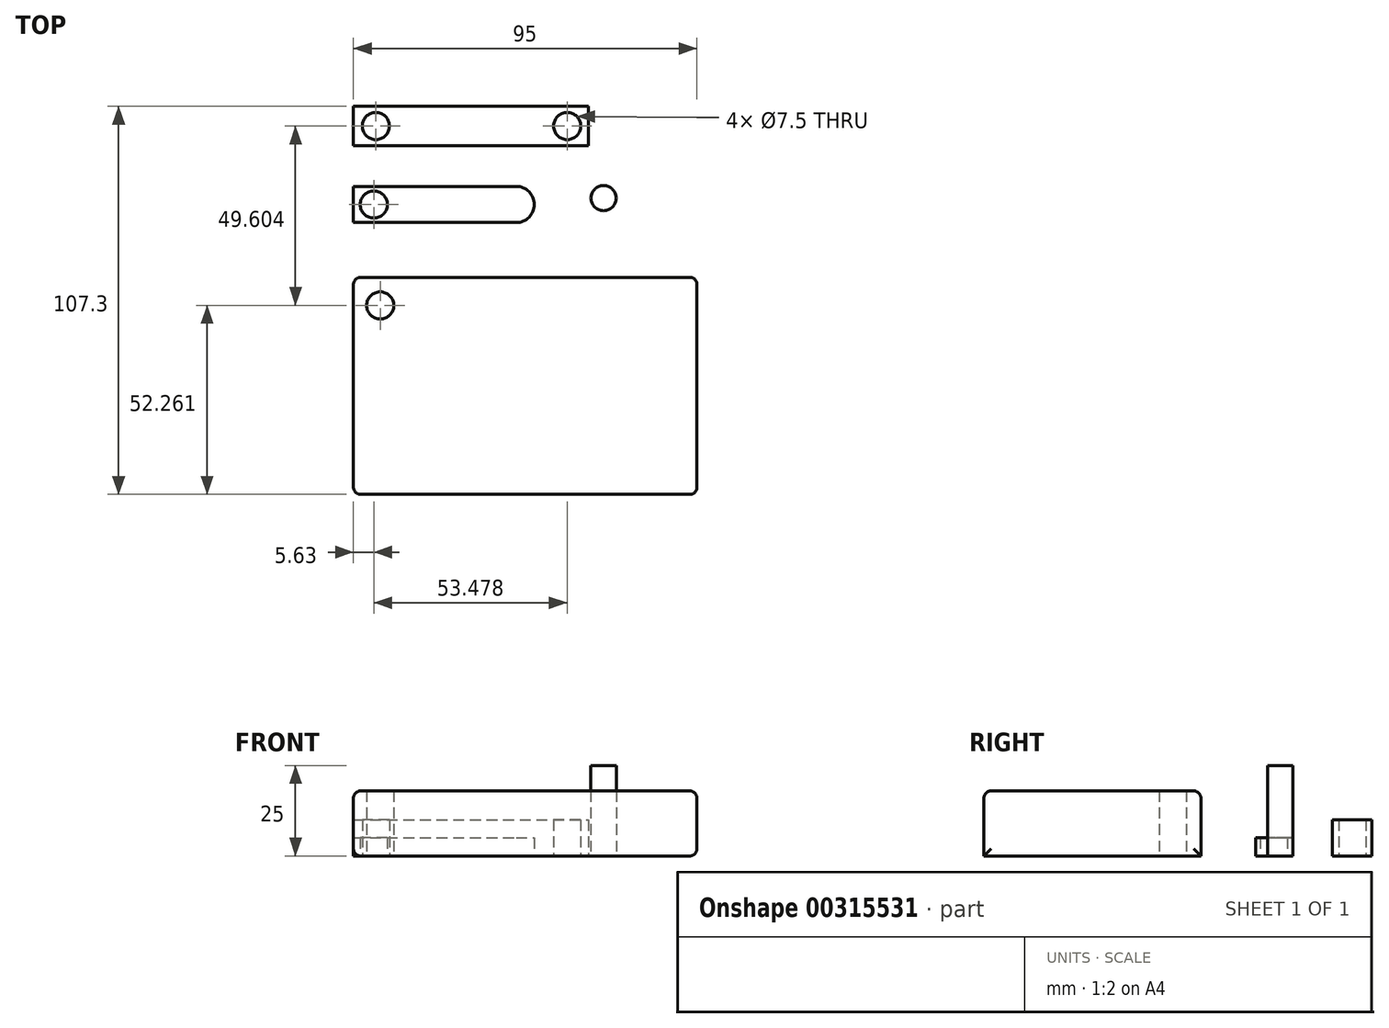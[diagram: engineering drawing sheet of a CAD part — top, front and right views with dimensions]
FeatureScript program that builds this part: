
annotation { "Feature Type Name" : "Feature", "Feature Type Description" : "" }
export const myFeature = defineFeature(function(context is Context, id is Id, definition is map)
    precondition{}
    {
        {
            var Q0;
            Q0=qCreatedBy(makeId("Top.planeOp"),FACE);
            var sketch = newSketch(context, id + "F0", { "sketchPlane" : qUnion([Q0])});
            skLineSegment(sketch, "E0.bottom", {"start": v(-53.3, 48.15) * mm, "end": v(-8.3, 48.15) * mm});
            skLineSegment(sketch, "E0.top", {"start": v(-53.3, 38.15) * mm, "end": v(-8.3, 38.15) * mm});
            skLineSegment(sketch, "E0.left", {"start": v(-53.3, 48.15) * mm, "end": v(-53.3, 38.15) * mm});
            skLineSegment(sketch, "E0.right", {"start": v(-3.3, 43.15) * mm, "end": v(-3.3, 43.15) * mm});
            skLineSegment(sketch, "E1.bottom", {"start": v(-53.3, 23) * mm, "end": v(41.7, 23) * mm});
            skLineSegment(sketch, "E1.top", {"start": v(-53.3, -37) * mm, "end": v(41.7, -37) * mm});
            skLineSegment(sketch, "E1.left", {"start": v(-53.3, 23) * mm, "end": v(-53.3, -37) * mm});
            skLineSegment(sketch, "E1.right", {"start": v(41.7, 23) * mm, "end": v(41.7, -37) * mm});
            skPoint(sketch, "E2.visualSharp", {"position": v(-3.3, 48.15) * mm});
            skArc(sketch, "E2.filletArc", {"start": v(-3.3, 43.15) * mm, "mid": v(-4.77, 46.69) * mm, "end": v(-8.3, 48.15) * mm});
            skPoint(sketch, "E3.visualSharp", {"position": v(-3.3, 38.15) * mm});
            skArc(sketch, "E3.filletArc", {"start": v(-8.3, 38.15) * mm, "mid": v(-4.77, 39.62) * mm, "end": v(-3.3, 43.15) * mm});
            skCircle(sketch, "E4", {"center": v(-47.68, 43.15) * mm, "radius": 3.75 * mm});
            skCircle(sketch, "E5", {"center": v(-45.9, 15.25) * mm, "radius": 3.75 * mm});
            skCircle(sketch, "E6", {"center": v(15.87, 44.93) * mm, "radius": 3.5 * mm});
            skLineSegment(sketch, "E7.bottom", {"start": v(-53.3, 70.3) * mm, "end": v(11.7, 70.3) * mm});
            skLineSegment(sketch, "E7.top", {"start": v(-53.3, 59.42) * mm, "end": v(11.7, 59.42) * mm});
            skLineSegment(sketch, "E7.left", {"start": v(-53.3, 70.3) * mm, "end": v(-53.3, 59.42) * mm});
            skLineSegment(sketch, "E7.right", {"start": v(11.7, 70.3) * mm, "end": v(11.7, 59.42) * mm});
            skCircle(sketch, "E8", {"center": v(-47.13, 64.85) * mm, "radius": 3.75 * mm});
            skPoint(sketch, "E8.centerSnap0", {"position": v(-53.3, 64.85) * mm});
            skCircle(sketch, "E9", {"center": v(5.8, 64.85) * mm, "radius": 3.75 * mm});
            skSolve(sketch);
        }
        {
            var Q0;
            Q0=makeQuery(id+"F0.imprint","IMPRINT",FACE,{"disambiguationData":[TD([[makeQuery(id+"F0.imprint","IMPRINT",EDGE,{"derivedFrom":sQuery(id+"F0.wireOp",EDGE,"E0.bottom")}),-1.0]])]});
            extrude(context, id + "F1", {"entities" : qUnion([Q0]), "depth" : 5 * mm});
        }
        {
            var Q0;
            Q0=makeQuery(id+"F0.imprint","IMPRINT",FACE,{"disambiguationData":[TD([[makeQuery(id+"F0.imprint","IMPRINT",EDGE,{"derivedFrom":sQuery(id+"F0.wireOp",EDGE,"E1.bottom")}),-1.0]])]});
            extrude(context, id + "F2", {"entities" : qUnion([Q0]), "depth" : 18 * mm});
        }
        {
            var Q0;
            Q0=makeQuery(id+"F0.imprint","IMPRINT",FACE,{"disambiguationData":[TD([[makeQuery(id+"F0.imprint","IMPRINT",EDGE,{"derivedFrom":sQuery(id+"F0.wireOp",EDGE,"E6")}),1.0]])]});
            extrude(context, id + "F3", {"entities" : qUnion([Q0]), "depth" : 25 * mm});
        }
        {
            var Q0;
            Q0=makeQuery(id+"F2.opExtrude","CAP_EDGE",EDGE,{"disambiguationData":[OSD([sQuery(id+"F0.wireOp",EDGE,"E1.bottom")])],"isStart":false});
            var Q1;
            Q1=makeQuery(id+"F2.opExtrude","CAP_EDGE",EDGE,{"disambiguationData":[OSD([sQuery(id+"F0.wireOp",EDGE,"E1.left")])],"isStart":false});
            var Q2;
            Q2=makeQuery(id+"F2.opExtrude","CAP_EDGE",EDGE,{"disambiguationData":[OSD([sQuery(id+"F0.wireOp",EDGE,"E1.right")])],"isStart":false});
            var Q3;
            Q3=makeQuery(id+"F2.opExtrude","CAP_EDGE",EDGE,{"disambiguationData":[OSD([sQuery(id+"F0.wireOp",EDGE,"E1.top")])],"isStart":false});
            var Q4;
            Q4=makeQuery(id+"F2.opExtrude","SWEPT_EDGE",EDGE,{"disambiguationData":[OSD([sQuery(id+"F0.wireOp",EDGE,"E1.bottom"),sQuery(id+"F0.wireOp",EDGE,"E1.left")])]});
            var Q5;
            Q5=makeQuery(id+"F2.opExtrude","SWEPT_FACE",FACE,{"disambiguationData":[OSD([sQuery(id+"F0.wireOp",EDGE,"E1.left")])]});
            var Q6;
            Q6=makeQuery(id+"F2.opExtrude","SWEPT_FACE",FACE,{"disambiguationData":[OSD([sQuery(id+"F0.wireOp",EDGE,"E1.right")])]});
            var Q7;
            Q7=makeQuery(id+"F2.opExtrude","SWEPT_EDGE",EDGE,{"disambiguationData":[OSD([sQuery(id+"F0.wireOp",EDGE,"E1.top"),sQuery(id+"F0.wireOp",EDGE,"E1.right")])]});
            fillet(context, id + "F4", {"entities" : qUnion([Q0, Q1, Q2, Q3, Q4, Q5, Q6, Q7]), "radius" : 2 * mm, "tangentPropagation" : true, "allowEdgeOverflow" : false});
        }
        {
            var Q0;
            Q0=makeQuery(id+"F0.imprint","IMPRINT",FACE,{"disambiguationData":[TD([[makeQuery(id+"F0.imprint","IMPRINT",EDGE,{"derivedFrom":sQuery(id+"F0.wireOp",EDGE,"E7.bottom")}),-1.0]])]});
            extrude(context, id + "F5", {"entities" : qUnion([Q0]), "depth" : 10 * mm});
        }
    });
